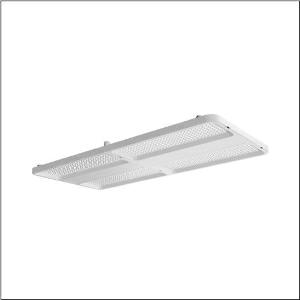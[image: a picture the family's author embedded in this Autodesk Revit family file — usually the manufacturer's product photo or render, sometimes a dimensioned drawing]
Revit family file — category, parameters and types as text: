
# Revit family: highbay_21_maxi_52hn12db5lda
name_source: partatom
category: Lighting Fixtures
units: mm (PartAtom-declared; Revit-internal decimal feet)

## family parameters
Cut with Voids When Loaded = No
Host = Face
Light Source = No
Part Type = Normal
Room Calculation Point = No
Round Connector Dimension = Use Diameter
Shared = No

## types (1)
- --- (1 x LED, 4120 lm, 22.6 W, 5000K)
    Apparent Load = 23 VA
    CIE Flux Codes = 90 98 100 100 100
    Color Rendering = 80
    Color Temperature = 5000K
    Default Elevation = 1800 mm
    Description = high bay luminaire Highbay 21 maxi; direct symmetric wide distribution, light control with lens of PMMA; UGR ≤ 22 (X = 4H | Y = 8H | S = 0.25H | reflection values 70/50/20); luminous flux: 27.240lm; light colour: 850, colour temperature: 5000K, MacAdam ≤ 3 SDCM (initial), colour rendering: CRI > 80; luminous efficacy: 189,2lm/W; rated service life: 75.000h (L80) at AT= ta max; control: DALI 2; luminaire connection: terminal, 5-pole, max. 2.5mm² (cable entry for one cable, Ø 8.5..16mm); mains connection: 230..240V, AC/DC 0/50..60Hz; connected load: 144W; protection rating (complete): IP66; insulation class (complete): insulation class I (protective earthing); protection symbol: D; impact resistance: IK08; certification: CE, ENEC, VDE, UKCA; luminaire for central battery installations according to EN 60598-2-22, internal wiring halogen-free; luminaire LABS conformity tested according to VDMA 24364:2018-05; Suitable for use in the food industry according to the specifications of IFS-Food, HACCP and/or BRC; housing frame of high-performance plastic PA6, matt traffic white (RAL 9016); cover of PMMA; dimension (LxWxH): 946 x 442 x 72mm; permissible operating ambient temperature: -40..+65°C (reducing of maximum allowable ambient temperature of 5°C with ceiling mounting); packaging unit: 1 piece; (delivery without accessories; please order mounting accessories separately)
    Height = 72 mm  [stored 0.23622 ft]
    Lamp = 1 x LED
    Lamp Light Flux = 4120 lm
    Lamp Power = 22.6 W
    Lamp count = 1
    Length = 946 mm
    Luminous efficacy = 182 lm/W
    Manufacturer = Siteco
    ModVariant = No
    Model = 52HN12DB5LDA
    Mounting Place = Ceiling
    Mounting Type = Pendant
    Number of Poles = 1
    OnlyDefault = Yes
    Power Factor = 1
    Product Name = Highbay 21 maxi
    Product group = high bay luminaire
    ProductGroupID = 902
    Protection Class = Protection class I
    Protection Degree = IP 66
    RLX_Detail_Level = 1
    RLX_Emergency_Light_Flux = 0 lm
    RLX_Emergency_Type = 0
    RLX_Emergency_Type_DB = No
    RlxData = <blob elided: 128021 chars, md5=1fade1f1>
    Socket = socket
    Standby Power = 0 W
    System Light Flux = 4120 lm
    System Power = 23 W
    Type Comments = : DC mode (central or group accumulator) initial emergency light level
    Type Image = l_1363244.jpg
    URL = http://relux.com
    VarID = @adj_004885
    Voltage = 0 V
    Weight = 0.00 kg
    Width = 442 mm

note: [stored X ft] marks values corroborated as IEEE doubles in the binary element streams (Revit-internal decimal feet)

## geometry (parser evidence)
native form markers: Blend x4, Sweep x10
no freeform markers — native parametric forms only
